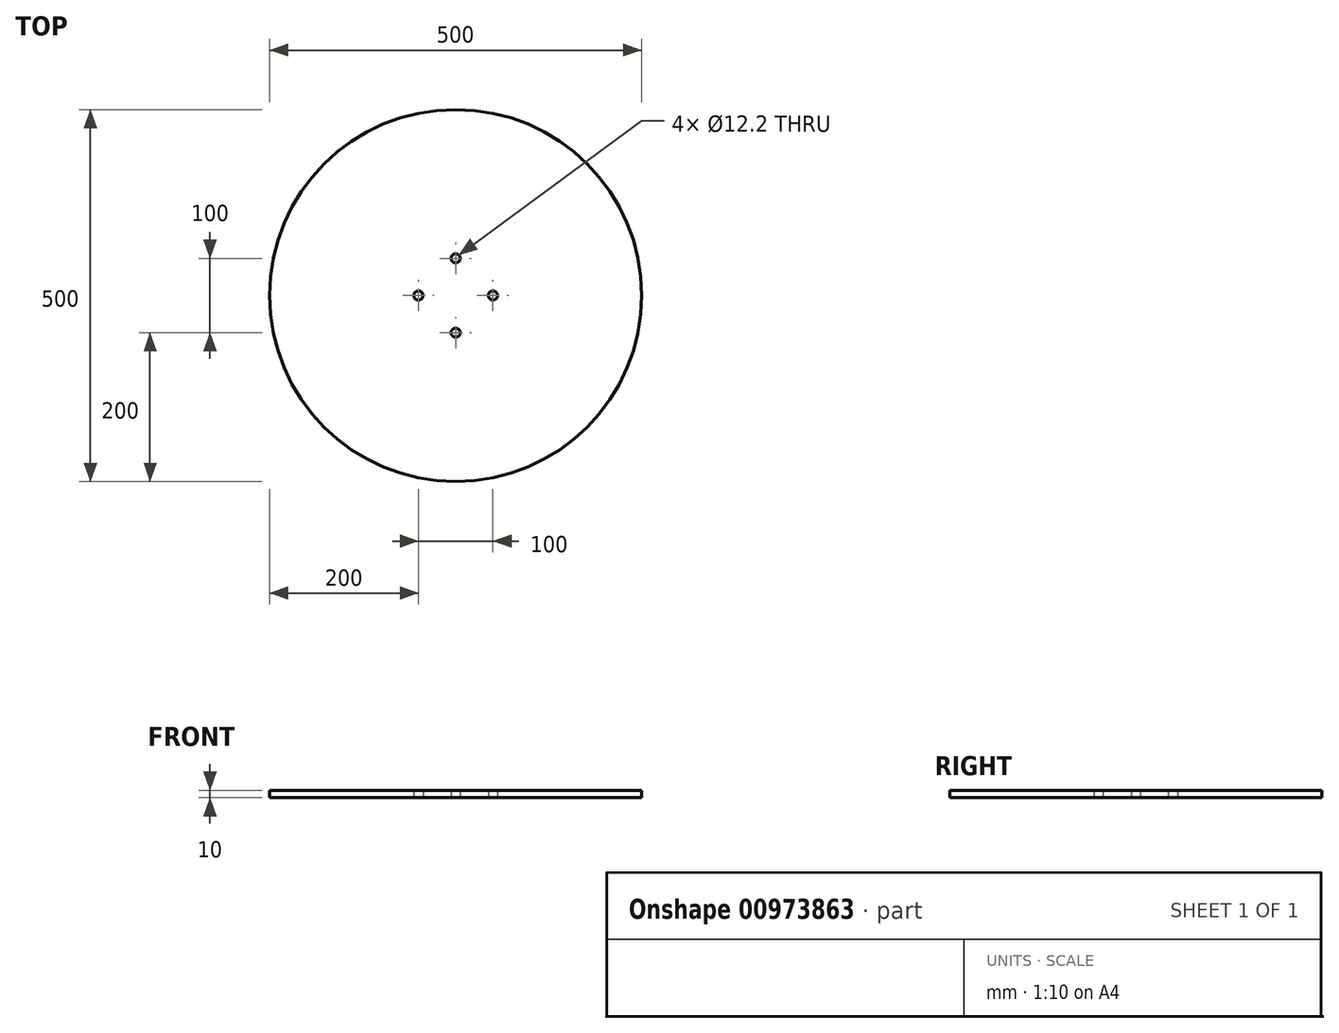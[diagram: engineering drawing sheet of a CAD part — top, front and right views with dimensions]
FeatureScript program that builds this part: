
annotation { "Feature Type Name" : "Feature", "Feature Type Description" : "" }
export const myFeature = defineFeature(function(context is Context, id is Id, definition is map)
    precondition{}
    {
        {
            var Q0;
            Q0=qCreatedBy(makeId("Top.planeOp"),FACE);
            var sketch = newSketch(context, id + "F0", { "sketchPlane" : qUnion([Q0])});
            skCircle(sketch, "E0", {"center": v(0, 0) * mm, "radius": 250 * mm});
            skCircle(sketch, "E1", {"center": v(0, 50) * mm, "radius": 6.1 * mm});
            skCircle(sketch, "E2.1.0", {"center": v(-50, 0) * mm, "radius": 6.1 * mm});
            skCircle(sketch, "E2.2.0", {"center": v(0, -50) * mm, "radius": 6.1 * mm});
            skCircle(sketch, "E2.3.0", {"center": v(50, 0) * mm, "radius": 6.1 * mm});
            skSolve(sketch);
        }
        {
            var Q0;
            Q0=makeQuery(id+"F0.imprint","IMPRINT",FACE,{"disambiguationData":[TD([[makeQuery(id+"F0.imprint","IMPRINT",EDGE,{"derivedFrom":sQuery(id+"F0.wireOp",EDGE,"E0")}),1.0]])]});
            extrude(context, id + "F1", {"entities" : qUnion([Q0]), "depth" : 10 * mm, "offsetDistance" : 25.4 * mm});
        }
    });
